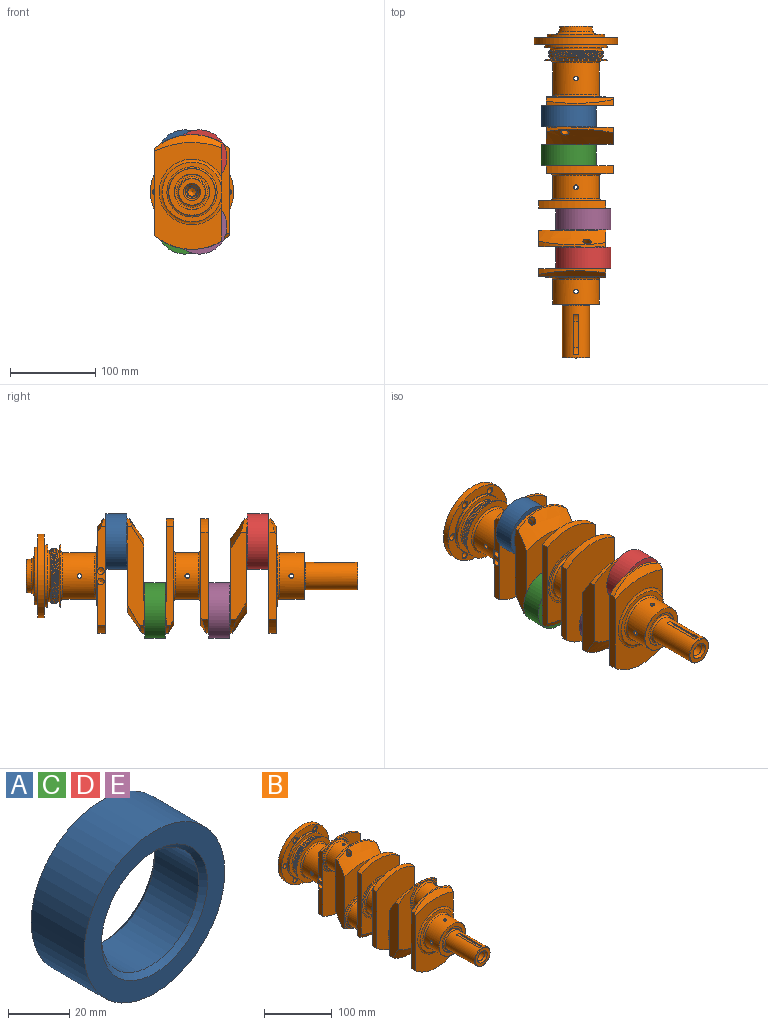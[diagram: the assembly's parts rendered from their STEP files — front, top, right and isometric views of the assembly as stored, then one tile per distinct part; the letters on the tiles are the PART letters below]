
ASSEMBLY  parts=5 mates=4
PART A: 6 faces, bbox 65x24.5x65 mm
  f0: cylinder r=22.5mm len=45mm, axis (0,1,0), area 2898.1mm2, adj f4,f5
  f1: cylinder r=32.5mm len=65mm, axis (0,1,0), area 5003mm2, adj f2,f3
  f2: plane 65x65mm, normal (0,-1,0), area 1432.6mm2, adj f1,f5
  f3: plane 65x65mm, normal (0,1,0), area 1432.6mm2, adj f1,f4
  f4: cone r=24.5mm half-angle=45deg, axis (0,1,0), area 417.6mm2, adj f0,f3
  f5: cone r=22.5mm half-angle=45deg, axis (0,-1,0), area 417.6mm2, adj f0,f2
PART B: 297 faces, bbox 133.7x410.5x174 mm
  f0: cylinder r=32.5mm len=65mm, axis (0,-1,0), area 258.4mm2, adj f1,f294,f295,f296
  f1: bspline ~75.06x65mm, area 482.8mm2, adj f0,f2,f293,f294,f296
  f2: torus R=31.5mm, axis (0,-1,0), area 777.3mm2, adj f1,f3,f4,f7,f291,f292,f293,f294
  f3: cylinder r=30.75mm len=61.5mm, axis (0,1,0), area 283.4mm2, adj f2,f4,f295,f296
  f4: bspline ~75.06x65mm, area 482.8mm2, adj f2,f3,f5,f291,f296
  f5: cylinder r=32.5mm len=65mm, axis (0,-1,0), area 258.4mm2, adj f4,f6,f291,f292,f296
  f6: cone r=30.65mm half-angle=58.2deg, axis (0,1,0), area 20.9mm2, adj f5,f292,f296
  f7: plane 74x74mm, normal (0,-1,0), area 1183.6mm2, adj f2,f8
  f8: cylinder r=37mm len=74mm, axis (0,-1,0), area 813.7mm2, adj f7,f9
  f9: torus R=37.5mm, axis (0,-1,0), area 177.9mm2, adj f8,f10,f285,f286,f287,f288,f289,f290
  f10: bspline ~3.76x2.42mm, area 2.3mm2, adj f9,f11,f284
  f11: cylinder r=4.1mm len=8.2mm, axis (0,1,0), area 180.7mm2, adj f10,f12,f284
  f12: plane 98x98mm, normal (0,1,0), area 3486.8mm2, adj f11,f13,f14,f274,f276,f278,f280,f282
  f13: cylinder r=49mm len=98mm, axis (0,-1,0), area 2309.1mm2, adj f12,f290
  f14: torus R=34.5mm, axis (0,1,0), area 168.7mm2, adj f12,f15
  f15: cylinder r=34mm len=68mm, axis (0,-1,0), area 747.7mm2, adj f14,f16
  f16: cone r=34mm half-angle=45deg, axis (0,-1,0), area 149.9mm2, adj f15,f17
  f17: plane 67x67mm, normal (0,1,0), area 1711.3mm2, adj f16,f18
  f18: torus R=24.03mm, axis (0,-1,0), area 760.2mm2, adj f17,f19
  f19: cone r=19mm half-angle=10deg, axis (0,-1,0), area 652.6mm2, adj f18,f20
  f20: cone r=19.17mm half-angle=50deg, axis (0,-1,0), area 178.9mm2, adj f19,f21
  f21: plane 36x36mm, normal (0,1,0), area 194.2mm2, adj f20,f22
  f22: cone r=16.19mm half-angle=45deg, axis (0,1,0), area 165.2mm2, adj f21,f23
  f23: cylinder r=15mm len=30mm, axis (0,-1,0), area 217.5mm2, adj f22,f24
  f24: plane 31.5x31.5mm, normal (0,-1,0), area 72.5mm2, adj f23,f25
  f25: cylinder r=15.75mm len=31.5mm, axis (0,-1,0), area 128.6mm2, adj f24,f26
  f26: plane 31.5x31.5mm, normal (0,1,0), area 72.5mm2, adj f25,f27
  f27: cylinder r=15mm len=30mm, axis (0,-1,0), area 848.2mm2, adj f26,f28
  f28: plane 30.5x30.5mm, normal (0,-1,0), area 23.8mm2, adj f27,f29
  f29: cylinder r=15.25mm len=30.5mm, axis (0,-1,0), area 95.8mm2, adj f28,f30
  f30: plane 30.5x30.5mm, normal (0,1,0), area 114.9mm2, adj f29,f31
  f31: cylinder r=14mm len=28mm, axis (0,-1,0), area 545.4mm2, adj f30,f32
  f32: plane 28x28mm, normal (0,1,0), area 361.3mm2, adj f31,f33
  f33: cone r=9mm half-angle=60deg, axis (0,1,0), area 116.1mm2, adj f32,f34
  f34: cylinder r=7mm len=14mm, axis (0,-1,0), area 301.1mm2, adj f33,f35
  f35: torus R=6mm, axis (0,-1,0), area 65.5mm2, adj f34,f36
  f36: plane 12x12mm, normal (0,1,0), area 34.6mm2, adj f35,f37
  f37: cylinder r=5mm len=48mm, axis (0,-1,0), area 1303.9mm2, adj f36,f38,f265,f266,f267,f270,f271,f272
  f38: cylinder r=2.5mm len=22.84mm, axis (0,0,1), area 358.7mm2, adj f37,f39
  f39: bspline ~5.43x5.4mm, area 4.7mm2, adj f38,f40
  f40: cylinder r=27.5mm len=55mm, axis (0,-1,0), area 6473.6mm2, adj f39,f41,f42,f43,f50,f51
  f41: bspline ~5.43x5.4mm, area 4.7mm2, adj f40,f266
  f42: bspline ~5.43x5.4mm, area 4.7mm2, adj f40,f265
  f43: torus R=29.5mm, axis (0,-1,0), area 557.2mm2, adj f40,f44
  f44: plane 74x74mm, normal (0,-1,0), area 1566.9mm2, adj f43,f45
  f45: cylinder r=37mm len=74mm, axis (0,-1,0), area 232.5mm2, adj f44,f46
  f46: cone r=37mm half-angle=81.9deg, axis (0,-1,0), area 1364.4mm2, adj f45,f47
  f47: torus R=30.75mm, axis (0,-1,0), area 203.6mm2, adj f46,f48
  f48: cylinder r=30mm len=60mm, axis (0,-1,0), area 18.8mm2, adj f47,f49
  f49: torus R=30.75mm, axis (0,-1,0), area 205mm2, adj f48,f296
  f50: bspline ~5.44x5.4mm, area 4.7mm2, adj f40,f273
  f51: torus R=29.5mm, axis (0,1,0), area 557.2mm2, adj f40,f52
  f52: plane 70x70mm, normal (0,1,0), area 1114.5mm2, adj f51,f53
  f53: torus R=38.57mm, axis (0,1,0), area 852.4mm2, adj f52,f54,f260
  f54: plane 125.72x79mm, normal (0,1,0), area 4779mm2, adj f53,f55,f258,f259,f260
  f55: cylinder r=67.5mm len=79mm, axis (0,-1,0), area 741.3mm2, adj f54,f56,f258,f260
  f56: plane 154.99x99mm, normal (0,-1,0), area 7489.8mm2, adj f55,f57,f257,f258,f260
  f57: torus R=28.63mm, axis (0,1,0), area 3059.6mm2, adj f56,f58,f256,f257,f260
  f58: plane 52x52mm, normal (0,-1,0), area 238mm2, adj f57,f59
  f59: torus R=24.5mm, axis (0,1,0), area 458.5mm2, adj f58,f60
  f60: cylinder r=22.5mm len=45mm, axis (0,-1,0), area 2852.4mm2, adj f59,f61,f68,f70,f71
  f61: bspline ~4.91x4.17mm, area 6.2mm2, adj f60,f62
  f62: cylinder r=1.75mm len=20mm, axis (0.68,0,0.73), area 243.6mm2, adj f61,f63,f65,f66,f67
  f63: cone r=1.75mm half-angle=60deg, axis (0.68,0,0.73), area 1.8mm2, adj f62,f64,f65
  f64: cone r=0mm half-angle=59deg, axis (0.21,0,-0.98), area 0mm2, adj f63,f65
  f65: cylinder r=1.75mm len=28.83mm, axis (0.21,0,-0.98), area 301.6mm2, adj f62,f63,f64,f70
  f66: cylinder r=1.75mm len=0.11mm, axis (0.21,0,-0.98), area 0mm2, adj f62
  f67: cylinder r=1.75mm len=0.11mm, axis (0.21,0,-0.98), area 0mm2, adj f62
  f68: bspline ~4.15x4.12mm, area 5.7mm2, adj f60,f69
  f69: cylinder r=1.75mm len=18.13mm, axis (0.21,0,-0.98), area 177.8mm2, adj f68,f267
  f70: bspline ~4.54x4.17mm, area 6mm2, adj f60,f65
  f71: torus R=24.5mm, axis (0,1,0), area 458.5mm2, adj f60,f72
  f72: plane 52x52mm, normal (0,1,0), area 238mm2, adj f71,f73
  f73: torus R=28.63mm, axis (0,1,0), area 1623.7mm2, adj f72,f74,f253,f254,f255
  f74: plane 135.44x40.63mm, normal (-1,0,0), area 1938.3mm2, adj f73,f75,f80,f81,f82,f83,f84,f253
  f75: cone r=109mm half-angle=55deg, axis (0,1,0), area 2228.9mm2, adj f74,f76,f77,f80,f254
  f76: plane 103.41x20.53mm, normal (1,0,0), area 1734.4mm2, adj f75,f80,f83,f84,f254,f255
  f77: bspline ~9.55x8mm, area 8.4mm2, adj f75,f78
  f78: cylinder r=4.57mm len=13.41mm, axis (-0.15,-0.67,0.72), area 259.6mm2, adj f77,f79
  f79: plane 9.02x6.74mm, normal (-0.15,-0.67,0.72), area 13.6mm2, adj f78,f267
  f80: plane 110.36x79mm, normal (0,-1,0), area 5617.6mm2, adj f74,f75,f76,f81,f83
  f81: torus R=28.63mm, axis (0,1,0), area -278.2mm2, adj f74,f80,f82,f83
  f82: plane 29.31x26.4mm, normal (0,-1,0), area 15.1mm2, adj f74,f81,f83
  f83: cylinder r=67.5mm len=79mm, axis (0,-1,0), area 306.7mm2, adj f74,f76,f80,f81,f82,f84
  f84: cone r=109mm half-angle=55deg, axis (0,-1,0), area 2229.1mm2, adj f74,f76,f83,f85,f255
  f85: bspline ~9.55x8.01mm, area 8.4mm2, adj f84,f86
  f86: cylinder r=4.57mm len=13.43mm, axis (-0.15,0.67,-0.72), area 252.1mm2, adj f85,f87
  f87: plane 9.02x6.74mm, normal (-0.15,0.67,-0.72), area 13.6mm2, adj f86,f88
  f88: cylinder r=4.07mm len=59.29mm, axis (-0.15,0.67,-0.72), area 1812.7mm2, adj f87,f89,f155,f156,f157,f158,f159,f160
  f89: cylinder r=1.75mm len=18.13mm, axis (0.21,0,0.98), area 177.8mm2, adj f88,f90
  f90: bspline ~4.15x4.12mm, area 5.7mm2, adj f89,f91
  f91: cylinder r=22.5mm len=45mm, axis (0,-1,0), area 2852.5mm2, adj f90,f92,f100,f101,f104
  f92: bspline ~4.17x3.7mm, area 6mm2, adj f91,f93
  f93: cylinder r=1.75mm len=30.08mm, axis (0.21,0,0.98), area 308.8mm2, adj f92,f94,f95,f96,f97,f98,f99
  f94: cylinder r=1.75mm len=22.76mm, axis (-0.92,0,-0.39), area 233mm2, adj f93,f95,f100
  f95: cone r=0mm half-angle=59deg, axis (0.21,0,0.98), area 6.3mm2, adj f93,f94
  f96: cone r=1.75mm half-angle=60deg, axis (-0.92,0,-0.39), area 0mm2, adj f93,f97
  f97: cylinder r=1.75mm len=2.22mm, axis (-0.92,0,-0.39), area 1mm2, adj f93,f96
  f98: cone r=1.75mm half-angle=60deg, axis (-0.92,0,-0.39), area 0mm2, adj f93,f99
  f99: cylinder r=1.75mm len=2.22mm, axis (-0.92,0,-0.39), area 1mm2, adj f93,f98
  f100: bspline ~4.17x4.14mm, area 6.2mm2, adj f91,f94
  f101: torus R=24.5mm, axis (0,1,0), area 458.5mm2, adj f91,f102
  f102: plane 52x52mm, normal (0,-1,0), area 238mm2, adj f101,f103
  f103: torus R=28.63mm, axis (0,1,0), area 0mm2, adj f102
  f104: torus R=24.5mm, axis (0,1,0), area 458.5mm2, adj f91,f105
  f105: plane 52x52mm, normal (0,1,0), area 238mm2, adj f104,f106
  f106: torus R=28.63mm, axis (0,1,0), area 733.5mm2, adj f105,f107,f152,f153,f154
  f107: plane 135.43x29.31mm, normal (-1,0,0), area 1005.4mm2, adj f106,f108,f110,f151,f152,f153,f154
  f108: cylinder r=67.5mm len=79mm, axis (0,-1,0), area 741.3mm2, adj f107,f109,f110,f152
  f109: plane 102.4x8.77mm, normal (1,0,0), area 892.6mm2, adj f108,f110,f151,f152,f153
  f110: plane 125.72x79mm, normal (0,-1,0), area 5596.5mm2, adj f107,f108,f109,f111,f151
  f111: torus R=34.68mm, axis (0,1,0), area 475.7mm2, adj f110,f112
  f112: plane 65x65mm, normal (0,-1,0), area 584.3mm2, adj f111,f113
  f113: torus R=29.5mm, axis (0,1,0), area 557.2mm2, adj f112,f114
  f114: cylinder r=27.5mm len=55mm, axis (0,1,0), area 4576.8mm2, adj f113,f115,f116,f121,f122,f150
  f115: bspline ~5.43x5.4mm, area 4.7mm2, adj f114,f155
  f116: bspline ~5.44x5.4mm, area 4.7mm2, adj f114,f117
  f117: cylinder r=2.5mm len=22.66mm, axis (0,0,1), area 332.4mm2, adj f116,f118,f119,f120,f156
  f118: cone r=4.07mm half-angle=60deg, axis (-0.15,0.67,-0.72), area 60mm2, adj f117,f119
  f119: cylinder r=4.07mm len=8.86mm, axis (-0.15,0.67,-0.72), area 58.2mm2, adj f117,f118,f155,f156,f157,f161
  f120: cone r=4.07mm half-angle=60deg, axis (0.15,-0.67,-0.72), area 60mm2, adj f117,f156
  f121: bspline ~5.43x5.4mm, area 4.7mm2, adj f114,f157
  f122: torus R=29.5mm, axis (0,-1,0), area 557.2mm2, adj f114,f123
  f123: plane 65x65mm, normal (0,1,0), area 584.3mm2, adj f122,f124
  f124: torus R=34.68mm, axis (0,-1,0), area 475.7mm2, adj f123,f125
  f125: plane 125.72x79mm, normal (0,1,0), area 5596.5mm2, adj f124,f126,f147,f148,f149
  f126: plane 135.43x29.31mm, normal (1,0,0), area 1005.4mm2, adj f125,f127,f128,f145,f146,f147,f149
  f127: plane 29.31x26.4mm, normal (0,-1,0), area 15.1mm2, adj f126,f128,f146
  f128: torus R=28.63mm, axis (0,-1,0), area 733.5mm2, adj f126,f127,f129,f145,f146
  f129: plane 52x52mm, normal (0,-1,0), area 238mm2, adj f128,f130
  f130: torus R=24.5mm, axis (0,-1,0), area 458.5mm2, adj f129,f131
  f131: cylinder r=22.5mm len=45mm, axis (0,1,0), area 2852.9mm2, adj f130,f132,f139,f141,f142
  f132: bspline ~4.54x4.17mm, area 6mm2, adj f131,f133
  f133: cylinder r=1.75mm len=28.83mm, axis (-0.21,0,0.98), area 301.6mm2, adj f132,f134,f137,f138
  f134: cylinder r=1.75mm len=20mm, axis (-0.68,0,-0.73), area 243.6mm2, adj f133,f135,f136,f137,f141
  f135: cylinder r=1.75mm len=0.11mm, axis (-0.21,0,0.98), area 0mm2, adj f134
  f136: cylinder r=1.75mm len=0.11mm, axis (-0.21,0,0.98), area 0mm2, adj f134
  f137: cone r=1.75mm half-angle=60deg, axis (-0.68,0,-0.73), area 1.8mm2, adj f133,f134,f138
  f138: cone r=0mm half-angle=59deg, axis (-0.21,0,0.98), area 0mm2, adj f133,f137
  f139: bspline ~4.15x4.12mm, area 5.7mm2, adj f131,f140
  f140: cylinder r=1.75mm len=18.13mm, axis (-0.21,0,0.98), area 177.8mm2, adj f139,f161
  f141: bspline ~4.91x4.17mm, area 6.2mm2, adj f131,f134
  f142: torus R=24.5mm, axis (0,-1,0), area 458.5mm2, adj f131,f143
  f143: plane 52x52mm, normal (0,1,0), area 238mm2, adj f142,f144
  f144: torus R=28.63mm, axis (0,-1,0), area 0mm2, adj f143
  f145: plane 134.99x79mm, normal (0,-1,0), area 7489.8mm2, adj f126,f128,f146,f147,f148
  f146: cylinder r=67.5mm len=79mm, axis (0,1,0), area 306.7mm2, adj f126,f127,f128,f145,f148,f149
  f147: cylinder r=67.5mm len=79mm, axis (0,1,0), area 741.3mm2, adj f125,f126,f145,f148
  f148: plane 102.4x8.77mm, normal (-1,0,0), area 892.6mm2, adj f125,f145,f146,f147,f149
  f149: cone r=109mm half-angle=55deg, axis (0,-1,0), area 752.5mm2, adj f125,f126,f146,f148
  f150: bspline ~5.43x5.4mm, area 4.7mm2, adj f114,f160
  f151: cone r=109mm half-angle=55deg, axis (0,1,0), area 752.5mm2, adj f107,f109,f110,f153
  f152: plane 134.99x79mm, normal (0,1,0), area 7489.8mm2, adj f106,f107,f108,f109,f153
  f153: cylinder r=67.5mm len=79mm, axis (0,-1,0), area 306.7mm2, adj f106,f107,f109,f151,f152,f154
  f154: plane 29.31x26.4mm, normal (0,1,0), area 15.1mm2, adj f106,f107,f153
  f155: cylinder r=2.5mm len=23.76mm, axis (1,0,0), area 364.6mm2, adj f88,f115,f119,f156,f161
  f156: cylinder r=4.07mm len=8.86mm, axis (0.15,-0.67,-0.72), area 58.2mm2, adj f88,f117,f119,f120,f155,f157
  f157: cylinder r=2.5mm len=23.76mm, axis (1,0,0), area 364.6mm2, adj f88,f119,f121,f156,f161
  f158: cone r=0mm half-angle=59deg, axis (0.21,0,0.98), area 8.8mm2, adj f88,f159
  f159: cylinder r=1.75mm len=3.9mm, axis (0.21,0,0.98), area 10.2mm2, adj f88,f158
  f160: cylinder r=2.5mm len=22.53mm, axis (0,0,1), area 318.7mm2, adj f88,f150,f161
  f161: cylinder r=4.07mm len=59.29mm, axis (0.15,-0.67,-0.72), area 1813.7mm2, adj f88,f119,f140,f155,f157,f160,f162,f251
  f162: plane 9.02x6.74mm, normal (0.15,-0.67,-0.72), area 13.6mm2, adj f161,f163
  f163: cylinder r=4.57mm len=13.41mm, axis (0.15,-0.67,-0.72), area 257.2mm2, adj f162,f164
  f164: bspline ~9.54x8mm, area 8.4mm2, adj f163,f165
  f165: cone r=109mm half-angle=55deg, axis (0,1,0), area 2228.7mm2, adj f164,f166,f248,f249,f250
  f166: cylinder r=67.5mm len=79mm, axis (0,1,0), area 306.7mm2, adj f165,f167,f168,f169,f248,f250
  f167: plane 29.31x26.4mm, normal (0,1,0), area 15.1mm2, adj f166,f168,f250
  f168: torus R=28.63mm, axis (0,-1,0), area -278.2mm2, adj f166,f167,f169,f250
  f169: plane 110.36x79mm, normal (0,1,0), area 5617.6mm2, adj f166,f168,f170,f248,f250
  f170: cone r=109mm half-angle=55deg, axis (0,-1,0), area 2228.7mm2, adj f169,f171,f247,f248,f250
  f171: cylinder r=67.5mm len=79mm, axis (0,1,0), area 306.7mm2, adj f170,f172,f173,f248,f249,f250
  f172: plane 9.31x6.4mm, normal (0,-1,0), area 15.1mm2, adj f171,f173,f250
  f173: torus R=28.63mm, axis (0,-1,0), area 1623.7mm2, adj f171,f172,f174,f249,f250
  f174: plane 52x52mm, normal (0,-1,0), area 238mm2, adj f173,f175
  f175: torus R=24.5mm, axis (0,-1,0), area 458.5mm2, adj f174,f176
  f176: cylinder r=22.5mm len=45mm, axis (0,1,0), area 2853.3mm2, adj f175,f177,f185,f245,f246
  f177: bspline ~4.17x4.14mm, area 6.2mm2, adj f176,f178
  f178: cylinder r=1.75mm len=22.76mm, axis (0.92,0,0.39), area 233mm2, adj f177,f179,f180
  f179: cone r=0mm half-angle=59deg, axis (-0.21,0,-0.98), area 6.3mm2, adj f178,f180
  f180: cylinder r=1.75mm len=30.08mm, axis (-0.21,0,-0.98), area 308.8mm2, adj f178,f179,f181,f182,f183,f184,f245
  f181: cone r=1.75mm half-angle=60deg, axis (0.92,0,0.39), area 0mm2, adj f180,f182
  f182: cylinder r=1.75mm len=2.22mm, axis (0.92,0,0.39), area 1mm2, adj f180,f181
  f183: cone r=1.75mm half-angle=60deg, axis (0.92,0,0.39), area 0mm2, adj f180,f184
  f184: cylinder r=1.75mm len=2.22mm, axis (0.92,0,0.39), area 1mm2, adj f180,f183
  f185: bspline ~4.15x4.12mm, area 5.7mm2, adj f176,f186
  f186: cylinder r=1.75mm len=18.13mm, axis (-0.21,0,-0.98), area 177.8mm2, adj f185,f187
  f187: cylinder r=4.07mm len=58.03mm, axis (0.15,0.67,0.72), area 1758.6mm2, adj f186,f188,f190,f191,f192,f243,f244
  f188: plane 9.02x6.74mm, normal (0.15,0.67,0.72), area 13.6mm2, adj f187,f189
  f189: cylinder r=4.57mm len=13.41mm, axis (0.15,0.67,0.72), area 253.5mm2, adj f188,f247
  f190: cone r=0mm half-angle=59deg, axis (-0.21,0,-0.98), area 8.8mm2, adj f187,f191
  f191: cylinder r=1.75mm len=3.9mm, axis (-0.21,0,-0.98), area 10.2mm2, adj f187,f190
  f192: cylinder r=2.5mm len=22.84mm, axis (0,0,1), area 351.6mm2, adj f187,f193,f244
  f193: bspline ~5.43x5.4mm, area 4.7mm2, adj f192,f194
  f194: cylinder r=27.5mm len=55mm, axis (0,-1,0), area 4970.4mm2, adj f193,f195,f197,f202,f225,f226
  f195: bspline ~5.43x5.4mm, area 4.7mm2, adj f194,f196
  f196: cylinder r=2.5mm len=22.84mm, axis (1,0,0), area 358.7mm2, adj f195,f244
  f197: bspline ~5.43x5.4mm, area 4.7mm2, adj f194,f198
  f198: cylinder r=2.5mm len=22.84mm, axis (1,0,0), area 353.1mm2, adj f197,f199,f244
  f199: cylinder r=4.07mm len=8.44mm, axis (0.15,0.67,0.72), area 24mm2, adj f198,f200,f201,f244
  f200: cylinder r=2.5mm len=21.37mm, axis (0,0,1), area 330.5mm2, adj f199,f201,f225
  f201: cone r=4.07mm half-angle=60deg, axis (0.15,0.67,0.72), area 21.6mm2, adj f199,f200,f244
  f202: cone r=27.3mm half-angle=45deg, axis (0,1,0), area 48.7mm2, adj f194,f203
  f203: plane 54.6x54.6mm, normal (0,-1,0), area 956mm2, adj f202,f204
  f204: torus R=20.5mm, axis (0,-1,0), area 102.7mm2, adj f203,f205
  f205: plane 41x41mm, normal (0,-1,0), area 302.4mm2, adj f204,f206
  f206: torus R=18mm, axis (0,-1,0), area 330.2mm2, adj f205,f207
  f207: cylinder r=16mm len=61mm, axis (0,-1,0), area 5853.4mm2, adj f206,f208,f212,f213,f214,f215,f216,f217
  f208: torus R=13.7mm, axis (1,0,0), area 3.6mm2, adj f207,f209,f212,f218
  f209: cylinder r=0.3mm len=31mm, axis (0,-1,0), area 14.6mm2, adj f208,f210,f212,f213
  f210: plane 31x5.4mm, normal (0,0,1), area 167.4mm2, adj f209,f211,f214,f218
  f211: cylinder r=0.3mm len=31mm, axis (0,1,0), area 14.6mm2, adj f210,f215,f216,f217
  f212: plane 44.98x1.92mm, normal (1,0,0), area 77.5mm2, adj f207,f208,f209,f213
  f213: torus R=13.7mm, axis (1,0,0), area 3.6mm2, adj f207,f209,f212,f214
  f214: cylinder r=14mm len=7.64mm, axis (-1,0,0), area 43.7mm2, adj f207,f210,f213,f215
  f215: torus R=13.7mm, axis (1,0,0), area 3.6mm2, adj f207,f211,f214,f216
  f216: plane 44.98x1.92mm, normal (-1,0,0), area 77.5mm2, adj f207,f211,f215,f217
  f217: torus R=13.7mm, axis (1,0,0), area 3.6mm2, adj f207,f211,f216,f218
  f218: cylinder r=14mm len=7.64mm, axis (-1,0,0), area 43.7mm2, adj f207,f208,f210,f217
  f219: cone r=15.5mm half-angle=45deg, axis (0,1,0), area 70mm2, adj f207,f220
  f220: plane 31x31mm, normal (0,-1,0), area 439.3mm2, adj f219,f221
  f221: cone r=8mm half-angle=30deg, axis (0,-1,0), area 228.8mm2, adj f220,f222
  f222: cylinder r=8mm len=18mm, axis (0,-1,0), area 904.8mm2, adj f221,f223
  f223: cone r=5.98mm half-angle=30deg, axis (0,-1,0), area 177.5mm2, adj f222,f224
  f224: plane 11.96x11.96mm, normal (0,-1,0), area 33.8mm2, adj f223,f244
  f225: bspline ~5.44x5.4mm, area 4.7mm2, adj f194,f200
  f226: torus R=29.5mm, axis (0,-1,0), area 557.2mm2, adj f194,f227
  f227: plane 70x70mm, normal (0,-1,0), area 1114.5mm2, adj f226,f228
  f228: torus R=38.57mm, axis (0,-1,0), area 852.4mm2, adj f227,f229,f238
  f229: plane 125.72x79mm, normal (0,-1,0), area 4779mm2, adj f228,f230,f236,f237,f238
  f230: cylinder r=67.5mm len=79mm, axis (0,1,0), area 741.3mm2, adj f229,f231,f236,f238
  f231: plane 154.99x99mm, normal (0,1,0), area 7489.8mm2, adj f230,f232,f235,f236,f238
  f232: torus R=28.63mm, axis (0,-1,0), area 3059.6mm2, adj f231,f233,f234,f235,f238
  f233: plane 52x52mm, normal (0,1,0), area 238mm2, adj f232,f246
  f234: plane 9.31x6.4mm, normal (0,1,0), area 15.1mm2, adj f232,f235,f238
  f235: cylinder r=67.5mm len=79mm, axis (0,1,0), area 306.7mm2, adj f231,f232,f234,f236,f237,f238
  f236: plane 102.4x8.77mm, normal (-1,0,0), area 892.6mm2, adj f229,f230,f231,f235,f237
  f237: cone r=109mm half-angle=55deg, axis (0,1,0), area 752.5mm2, adj f229,f235,f236,f238
  f238: plane 135.42x30.8mm, normal (1,0,0), area 929.3mm2, adj f228,f229,f230,f231,f232,f234,f235,f237
  f239: cylinder r=4mm len=13mm, axis (1,0,0), area 326.7mm2, adj f238,f240
  f240: cone r=0mm half-angle=59deg, axis (1,0,0), area 58.6mm2, adj f239
  f241: cylinder r=4mm len=13mm, axis (1,0,0), area 326.7mm2, adj f238,f242
  f242: cone r=0mm half-angle=59deg, axis (1,0,0), area 58.6mm2, adj f241
  f243: cone r=5mm half-angle=60deg, axis (0,-1,0), area 90.7mm2, adj f187,f244
  f244: cylinder r=5mm len=65mm, axis (0,-1,0), area 1857.4mm2, adj f187,f192,f196,f198,f199,f201,f224,f243
  f245: bspline ~4.17x3.7mm, area 6mm2, adj f176,f180
  f246: torus R=24.5mm, axis (0,-1,0), area 458.5mm2, adj f176,f233
  f247: bspline ~9.54x8mm, area 8.4mm2, adj f170,f189
  f248: plane 103.41x20.53mm, normal (-1,0,0), area 1734.4mm2, adj f165,f166,f169,f170,f171,f249
  f249: plane 130.36x99mm, normal (0,-1,0), area 5617.6mm2, adj f165,f171,f173,f248,f250
  f250: plane 135.44x40.63mm, normal (1,0,0), area 1938.3mm2, adj f165,f166,f167,f168,f169,f170,f171,f172
  f251: cone r=0mm half-angle=59deg, axis (-0.21,0,0.98), area 8.8mm2, adj f161,f252
  f252: cylinder r=1.75mm len=3.9mm, axis (-0.21,0,0.98), area 10.2mm2, adj f161,f251
  f253: plane 9.31x6.4mm, normal (0,1,0), area 15.1mm2, adj f73,f74,f254
  f254: cylinder r=67.5mm len=79mm, axis (0,-1,0), area 306.7mm2, adj f73,f74,f75,f76,f253,f255
  f255: plane 130.36x99mm, normal (0,1,0), area 5617.6mm2, adj f73,f74,f76,f84,f254
  f256: plane 9.31x6.4mm, normal (0,-1,0), area 15.1mm2, adj f57,f257,f260
  f257: cylinder r=67.5mm len=79mm, axis (0,-1,0), area 306.7mm2, adj f56,f57,f256,f258,f259,f260
  f258: plane 102.4x8.77mm, normal (1,0,0), area 892.6mm2, adj f54,f55,f56,f257,f259
  f259: cone r=109mm half-angle=55deg, axis (0,-1,0), area 752.5mm2, adj f54,f257,f258,f260
  f260: plane 135.42x30.8mm, normal (-1,0,0), area 929.3mm2, adj f53,f54,f55,f56,f57,f256,f257,f259
  f261: cylinder r=4mm len=13mm, axis (-1,0,0), area 326.7mm2, adj f260,f262
  f262: cone r=0mm half-angle=59deg, axis (-1,0,0), area 58.6mm2, adj f261
  f263: cylinder r=4mm len=13mm, axis (-1,0,0), area 326.7mm2, adj f260,f264
  f264: cone r=0mm half-angle=59deg, axis (-1,0,0), area 58.6mm2, adj f263
  f265: cylinder r=2.5mm len=22.84mm, axis (1,0,0), area 358.7mm2, adj f37,f42
  f266: cylinder r=2.5mm len=22.97mm, axis (1,0,0), area 354.4mm2, adj f37,f41,f271,f272
  f267: cylinder r=4.07mm len=58.03mm, axis (-0.15,-0.67,0.72), area 1764.8mm2, adj f37,f69,f79,f268,f269,f270
  f268: cone r=0mm half-angle=59deg, axis (0.21,0,-0.98), area 8.8mm2, adj f267,f269
  f269: cylinder r=1.75mm len=3.9mm, axis (0.21,0,-0.98), area 10.2mm2, adj f267,f268
  f270: cone r=5mm half-angle=60deg, axis (0,1,0), area 89.8mm2, adj f37,f267
  f271: cylinder r=4.07mm len=8.44mm, axis (-0.15,-0.67,0.72), area 33.4mm2, adj f37,f266,f272
  f272: cone r=4.07mm half-angle=60deg, axis (-0.15,-0.67,0.72), area 31.3mm2, adj f37,f266,f271,f273
  f273: cylinder r=2.5mm len=22.79mm, axis (0,0,1), area 353.5mm2, adj f37,f50,f272
  f274: cylinder r=4.1mm len=8.2mm, axis (0,1,0), area 180.3mm2, adj f12,f275,f285
  f275: cone r=4.6mm half-angle=45deg, axis (0,-1,0), area 16.3mm2, adj f274,f285,f290
  f276: cylinder r=4.1mm len=8.2mm, axis (0,1,0), area 180.3mm2, adj f12,f277,f286
  f277: cone r=4.6mm half-angle=45deg, axis (0,-1,0), area 16.3mm2, adj f276,f286,f290
  f278: cylinder r=4.1mm len=8.2mm, axis (0,1,0), area 180.3mm2, adj f12,f279,f287
  f279: cone r=4.6mm half-angle=45deg, axis (0,-1,0), area 16.3mm2, adj f278,f287,f290
  f280: cylinder r=4.1mm len=8.2mm, axis (0,1,0), area 180.3mm2, adj f12,f281,f288
  f281: cone r=4.6mm half-angle=45deg, axis (0,-1,0), area 16.3mm2, adj f280,f288,f290
  f282: cylinder r=4.1mm len=8.2mm, axis (0,1,0), area 180.7mm2, adj f12,f283,f289
  f283: cone r=4.6mm half-angle=45deg, axis (0,-1,0), area 16.3mm2, adj f282,f289,f290
  f284: cone r=4.6mm half-angle=45deg, axis (0,-1,0), area 16.3mm2, adj f10,f11,f290
  f285: bspline ~4.32x0.68mm, area 2.3mm2, adj f9,f274,f275
  f286: bspline ~3.76x2.42mm, area 2.3mm2, adj f9,f276,f277
  f287: bspline ~3.76x2.42mm, area 2.3mm2, adj f9,f278,f279
  f288: bspline ~4.32x0.68mm, area 2.3mm2, adj f9,f280,f281
  f289: bspline ~3.76x2.42mm, area 2.3mm2, adj f9,f282,f283
  f290: plane 98x98mm, normal (0,-1,0), area 2736.7mm2, adj f9,f13,f275,f277,f279,f281,f283,f284
  f291: cone r=32.5mm half-angle=55.6deg, axis (0,-1,0), area 95.2mm2, adj f2,f4,f5,f292
  f292: bspline ~75.06x65mm, area 482.5mm2, adj f2,f5,f6,f291,f293
  f293: cylinder r=30.75mm len=61.5mm, axis (0,1,0), area 283.4mm2, adj f1,f2,f292,f296
  f294: cone r=32.5mm half-angle=55.6deg, axis (0,-1,0), area 95.2mm2, adj f0,f1,f2,f295
  f295: bspline ~75.06x65mm, area 482.5mm2, adj f0,f2,f3,f294,f296
  f296: cone r=30.65mm half-angle=58.2deg, axis (0,1,0), area 214.7mm2, adj f0,f1,f3,f4,f5,f6,f49,f293
PART C: same geometry as A
PART D: same geometry as A
PART E: same geometry as A
PLACE A t=(-8.67,83.25,40.58)mm
PLACE B at identity
PLACE C t=(-8.67,37.75,-40.58)mm
PLACE D t=(8.67,-83.25,40.58)mm
PLACE E t=(8.67,-37.75,-40.58)mm
MATE revolute E.f0 <-> B.f128  axis (0,1,0) through (8.67,-37.75,-40.58)mm
MATE revolute D.f0 <-> B.f173  axis (0,1,0) through (8.67,-83.25,40.58)mm
MATE revolute C.f0 <-> B.f81  axis (0,1,0) through (-8.67,37.75,-40.58)mm
MATE revolute A.f0 <-> B.f57  axis (0,1,0) through (-8.67,83.25,40.58)mm
